# Revit family: Electronics_Expansion-Inputs_Biamp_Vocia_Paging-Station-Kit_PSKIT-1___
name_source: partatom
category: Communication Devices
units: mm (PartAtom-declared; Revit-internal decimal feet)

## family parameters
Cut with Voids When Loaded = No
Host = Face
Maintain Annotation Orientation = No
OmniClass Number = 23.85.10.11.14
OmniClass Title = Audio Equipment
Part Type = Normal
Room Calculation Point = No
Round Connector Dimension = Use Diameter
Shared = No

## types (1)
- PSKIT-1
    A/D Converters = 24-bit
    Altitude = 0-10,000 ft (0-3000m) MSL
    Apparent Load = 0 VA
    Compliance = FCC Part 15B (USA) CE marked (Europe) RCM (Australia) EAC (Eurasian Customs Union) RoHS Directive (Europe)
    Connector Description = PoE 802.3af Type 1 Class 2
    Default Elevation = 4' - 0"
    Depth = 0' - 11 17/32"
    Description = Vocia® PSKIT-1 Paging Station Kit
    Effective Input Headroom = 30dB
    Frequency Response = 100Hz ~ 20kHz: +0, -1dB
    Gain = Adjustable in 1dB steps over a 30dB range
    General Purpose Inputs Quantity = 12
    General Purpose Inputs TTL Logic High = 2-5V
    General Purpose Inputs TTL Logic Low = 0 – 0.8V
    General Purpose Inputs Type = Contact Closure / TTL
    General Purpose Outputs Max Continuous Current = 200mA
    General Purpose Outputs Max External Supply = 40V
    General Purpose Outputs Quantity = 3
    Height = 0' - 1 5/8"
    Housing Material = Biamp - Metal - Silver
    Humidity = 0-95% relative humidity (non-condensing)
    Manufacturer = Biamp
    Max Power Consumption = 0 W
    Model = Vocia PSKIT-1
    Network Connection = RJ45 with shielded Ethernet (CAT5, CAT5e, CAT6, or CAT7)
    Nominal Input Level = -50dBu
    Number of Poles = 1
    Power Factor = 1
    Product Documentation Link = https://downloads.biamp.com
    Product Page URL = https://www.biamp.com
    Product data url = https://www.bimobject.com
    RS-232 Baud = 57600 bps
    RS-232 Data Bits = 8
    RS-232 Flow Control = None
    RS-232 Parity = None
    RS-232 Stop Bits = 1
    Reference Output = 12V DC 100mA
    Sample Rate = 48kHz
    System Headroom = 18dB
    THD+N = 20Hz ~ 8kHz: <0.05%
    Temperature Range = 32 - 113° F (0 – 45° C)
    URL = https://www.biamp.com
    Voltage = 0 V
    Weight = 2.30 lbf
    Width = 0' - 5 1/4"

## geometry (parser evidence)
native form markers: Sweep x2
no freeform markers — native parametric forms only
